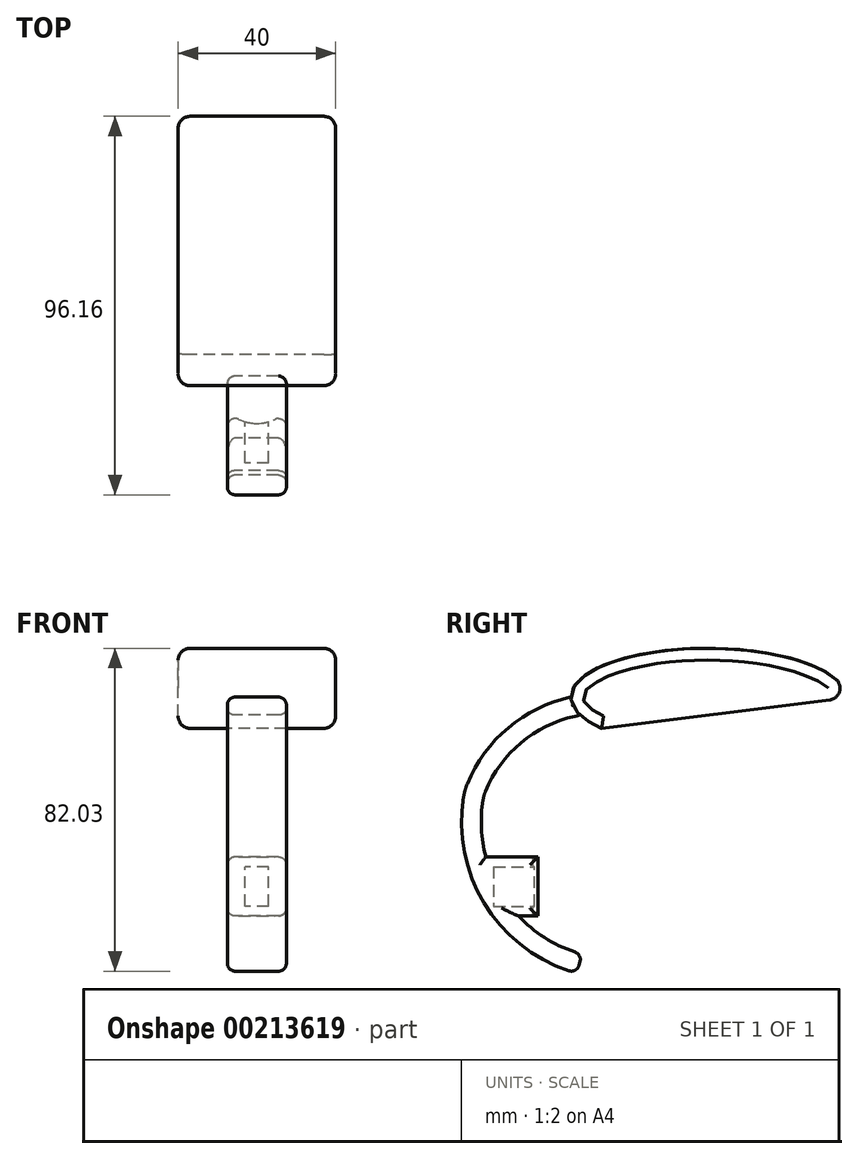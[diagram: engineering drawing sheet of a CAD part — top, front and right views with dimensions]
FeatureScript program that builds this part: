
annotation { "Feature Type Name" : "Feature", "Feature Type Description" : "" }
export const myFeature = defineFeature(function(context is Context, id is Id, definition is map)
    precondition{}
    {
        {
            var Q0;
            Q0=qCreatedBy(makeId("Right.planeOp"),FACE);
            var sketch = newSketch(context, id + "F0", { "sketchPlane" : qUnion([Q0])});
            skPoint(sketch, "E0", {"position": v(-25.02, -24.7) * mm});
            skPoint(sketch, "E1", {"position": v(-49.96, 15.62) * mm});
            skPoint(sketch, "E2", {"position": v(-17.82, 36.4) * mm});
            skPoint(sketch, "E3", {"position": v(-45.62, -9.14) * mm});
            skPoint(sketch, "E4", {"position": v(-37.55, 31.22) * mm});
            skArc(sketch, "E5", {"start": v(-50.16, 14.52) * mm, "mid": v(-45.13, -9.93) * mm, "end": v(-25.02, -24.7) * mm});
            skArc(sketch, "E6", {"start": v(-26.84, 35.73) * mm, "mid": v(-40.53, 29) * mm, "end": v(-49.54, 16.68) * mm});
            skArc(sketch, "E7.filletArc", {"start": v(-49.54, 16.68) * mm, "mid": v(-49.91, 15.62) * mm, "end": v(-50.16, 14.52) * mm});
            skArc(sketch, "E8.0", {"start": v(-27.9, 40.62) * mm, "mid": v(-43.75, 32.83) * mm, "end": v(-54.17, 18.59) * mm});
            skArc(sketch, "E9.0", {"start": v(-55.1, 15.33) * mm, "mid": v(-49.34, -12.62) * mm, "end": v(-26.34, -29.53) * mm});
            skArc(sketch, "E9.1", {"start": v(-54.17, 18.59) * mm, "mid": v(-54.72, 16.99) * mm, "end": v(-55.1, 15.33) * mm});
            skLineSegment(sketch, "E10", {"start": v(-26.34, -29.53) * mm, "end": v(-25.02, -24.7) * mm});
            skLineSegment(sketch, "E11", {"start": v(-26.84, 35.73) * mm, "end": v(22, 46.42) * mm});
            skLineSegment(sketch, "E12.0", {"start": v(-27.9, 40.62) * mm, "end": v(20.94, 51.3) * mm});
            skLineSegment(sketch, "E13", {"start": v(20.94, 51.3) * mm, "end": v(22, 46.42) * mm});
            skEllipticalArc(sketch, "E14", {});
            skLineSegment(sketch, "E15", {"start": v(-20.03, 32.68) * mm, "end": v(42.1, 40.43) * mm});
            skPoint(sketch, "E15.endSnap0", {"position": v(42.1, 40.4) * mm});
            skLineSegment(sketch, "E16", {"start": v(-46.55, -7.5) * mm, "end": v(-34.49, -7.5) * mm, "construction": true});
            skLineSegment(sketch, "E17.bottom", {"start": v(-49.49, 0) * mm, "end": v(-34.49, 0) * mm});
            skLineSegment(sketch, "E17.right", {"start": v(-34.49, 0) * mm, "end": v(-34.49, -15) * mm});
            skLineSegment(sketch, "E18.trimOffspring", {"start": v(-41.17, -15) * mm, "end": v(-34.49, -15) * mm});
            const initialGuessF0  = {"E14": [0.007094516884535551, 0.040509749203920364, -0.9999952117273706, 0.0030945956652309804, 0.035, 0.0125, 3.141592653589793, 0.6850566038234638]};
            skSetInitialGuess(sketch, initialGuessF0);
            skSolve(sketch);
        }
        {
            var Q0;
            Q0=makeQuery(id+"F0.imprint","IMPRINT",FACE,{"disambiguationData":[TD([[makeQuery(id+"F0.imprint","IMPRINT",EDGE,{"derivedFrom":sQuery(id+"F0.wireOp",EDGE,"E5")}),-1.0]])]});
            var Q1;
            {var subQ0=sQuery(id+"F0.wireOp",EDGE,"E17.bottom");Q1=makeQuery(id+"F0.imprint","IMPRINT",FACE,{"disambiguationData":[TD([[makeQuery(id+"F0.imprint","IMPRINT",EDGE,{"derivedFrom":subQ0}),-1.0]])]});}
            extrude(context, id + "F1", {"entities" : qUnion([Q0, Q1]), "endBound" : BoundingType.SYMMETRIC, "depth" : 15 * mm});
        }
        {
            var Q0;
            {var subQ4=sQuery(id+"F0.wireOp",EDGE,"E12.0");Q0=makeQuery(id+"F0.imprint","IMPRINT",FACE,{"disambiguationData":[TD([[makeQuery(id+"F0.imprint","IMPRINT",EDGE,{"derivedFrom":subQ4}),1.0]])]});}
            var Q1;
            {var subQ4=sQuery(id+"F0.wireOp",EDGE,"E12.0");Q1=makeQuery(id+"F0.imprint","IMPRINT",FACE,{"disambiguationData":[TD([[makeQuery(id+"F0.imprint","IMPRINT",EDGE,{"derivedFrom":subQ4}),-1.0]])]});}
            extrude(context, id + "F2", {"entities" : qUnion([Q0, Q1]), "operationType" : NewBodyOperationType.ADD, "endBound" : BoundingType.SYMMETRIC, "depth" : 40 * mm});
        }
        {
            var Q0;
            Q0=makeQuery(id+"F1.opExtrude","SWEPT_EDGE",EDGE,{"disambiguationData":[OSD([sQuery(id+"F0.wireOp",EDGE,"E5"),sQuery(id+"F0.wireOp",EDGE,"E10")])]});
            var Q1;
            Q1=makeQuery(id+"F1.opExtrude","SWEPT_EDGE",EDGE,{"disambiguationData":[OSD([sQuery(id+"F0.wireOp",EDGE,"E9.0"),sQuery(id+"F0.wireOp",EDGE,"E10")])]});
            var Q2;
            Q2=makeQuery(id+"F1.opExtrude","CAP_EDGE",EDGE,{"disambiguationData":[OSD([sQuery(id+"F0.wireOp",EDGE,"E10")])],"isStart":false});
            var Q3;
            Q3=makeQuery(id+"F1.opExtrude","CAP_EDGE",EDGE,{"disambiguationData":[OSD([sQuery(id+"F0.wireOp",EDGE,"E10")])],"isStart":true});
            var Q4;
            Q4=makeQuery(id+"F1.opExtrude","CAP_EDGE",EDGE,{"disambiguationData":[OSD([sQuery(id+"F0.wireOp",EDGE,"E9.0")])],"isStart":false});
            var Q5;
            Q5=makeQuery(id+"F1.opExtrude","CAP_EDGE",EDGE,{"disambiguationData":[OSD([sQuery(id+"F0.wireOp",EDGE,"E5")])],"isStart":false});
            var Q6;
            Q6=makeQuery(id+"F1.opExtrude","CAP_EDGE",EDGE,{"disambiguationData":[OSD([sQuery(id+"F0.wireOp",EDGE,"E5")])],"isStart":true});
            var Q7;
            Q7=makeQuery(id+"F1.opExtrude","CAP_EDGE",EDGE,{"disambiguationData":[OSD([sQuery(id+"F0.wireOp",EDGE,"E9.0")])],"isStart":true});
            fillet(context, id + "F3", {"entities" : qUnion([Q0, Q1, Q2, Q3, Q4, Q5, Q6, Q7]), "radius" : 2 * mm, "tangentPropagation" : true, "allowEdgeOverflow" : false});
        }
        {
            var Q0;
            Q0=makeQuery(id+"F2.opExtrude","CAP_EDGE",EDGE,{"disambiguationData":[OSD([sQuery(id+"F0.wireOp",EDGE,"E14")])],"isStart":false});
            var Q1;
            Q1=makeQuery(id+"F2.opExtrude","CAP_EDGE",EDGE,{"disambiguationData":[OSD([sQuery(id+"F0.wireOp",EDGE,"E14")])],"isStart":true});
            var Q2;
            {var subQ0=sQuery(id+"F0.wireOp",EDGE,"E15");var subQ1=sQuery(id+"F0.wireOp",EDGE,"E14");Q2=makeQuery(id+"F2.opExtrude","SWEPT_EDGE",EDGE,{"disambiguationData":[OSD([subQ1,subQ0]),TDD([makeQuery(id+"F0.imprint","INTERSECT",VERTEX,{"disambiguationData":[OD(1.0)],"derivedFrom":[subQ1,subQ0]})])]});}
            var Q3;
            Q3=makeQuery(id+"F1.opExtrude","SWEPT_EDGE",EDGE,{"disambiguationData":[OSD([sQuery(id+"F0.wireOp",EDGE,"E8.0"),sQuery(id+"F0.wireOp",EDGE,"E12.0"),sQuery(id+"F0.wireOp",EDGE,"E14")])]});
            var Q4;
            Q4=makeQuery(id+"F1.opExtrude","SWEPT_EDGE",EDGE,{"disambiguationData":[OSD([sQuery(id+"F0.wireOp",EDGE,"E11"),sQuery(id+"F0.wireOp",EDGE,"E14")])]});
            var Q5;
            Q5=makeQuery(id+"F1.opExtrude","CAP_EDGE",EDGE,{"disambiguationData":[OSD([sQuery(id+"F0.wireOp",EDGE,"E14")])],"isStart":false});
            var Q6;
            Q6=makeQuery(id+"F1.opExtrude","CAP_EDGE",EDGE,{"disambiguationData":[OSD([sQuery(id+"F0.wireOp",EDGE,"E14")])],"isStart":true});
            var Q7;
            Q7=makeQuery(id+"F2.opExtrude","CAP_EDGE",EDGE,{"disambiguationData":[OSD([sQuery(id+"F0.wireOp",EDGE,"E15")])],"isStart":false});
            var Q8;
            Q8=makeQuery(id+"F2.opExtrude","CAP_EDGE",EDGE,{"disambiguationData":[OSD([sQuery(id+"F0.wireOp",EDGE,"E15")])],"isStart":true});
            fillet(context, id + "F4", {"entities" : qUnion([Q0, Q1, Q2, Q3, Q4, Q5, Q6, Q7, Q8]), "radius" : 3 * mm, "tangentPropagation" : true, "allowEdgeOverflow" : false});
        }
        {
            var Q0;
            Q0=makeQuery(id+"F1.opExtrude","SWEPT_FACE",FACE,{"disambiguationData":[OSD([sQuery(id+"F0.wireOp",EDGE,"E17.right")])]});
            var sketch = newSketch(context, id + "F5", { "sketchPlane" : qUnion([Q0])});
            skLineSegment(sketch, "E19.bottom", {"start": v(-3, -2.5) * mm, "end": v(3, -2.5) * mm});
            skLineSegment(sketch, "E19.top", {"start": v(-3, -12.5) * mm, "end": v(3, -12.5) * mm});
            skLineSegment(sketch, "E19.left", {"start": v(-3, -2.5) * mm, "end": v(-3, -12.5) * mm});
            skLineSegment(sketch, "E19.right", {"start": v(3, -2.5) * mm, "end": v(3, -12.5) * mm});
            skPoint(sketch, "E19.middle", {"position": v(0, -7.5) * mm});
            skSolve(sketch);
        }
        {
            var Q0;
            Q0 = qSketchRegion(id + "F5", true);
            extrude(context, id + "F6", {"entities" : qUnion([Q0]), "operationType" : NewBodyOperationType.REMOVE, "oppositeDirection" : true, "depth" : 13 * mm});
        }
        {
            var Q0;
            Q0=makeQuery(id+"F1.opExtrude","SWEPT_FACE",FACE,{"disambiguationData":[OSD([sQuery(id+"F0.wireOp",EDGE,"E17.bottom")])]});
            var sketch = newSketch(context, id + "F7", { "sketchPlane" : qUnion([Q0])});
            skLineSegment(sketch, "E20", {"start": v(0, -34.49) * mm, "end": v(0, -37.49) * mm, "construction": true});
            skArc(sketch, "E21", {"start": v(-7.5, -34.49) * mm, "mid": v(0, -37.49) * mm, "end": v(7.5, -34.49) * mm});
            skLineSegment(sketch, "E22", {"start": v(-7.5, -34.49) * mm, "end": v(7.5, -34.49) * mm});
            skSolve(sketch);
        }
        {
            var Q0;
            Q0 = qSketchRegion(id + "F7", true);
            extrude(context, id + "F8", {"entities" : qUnion([Q0]), "operationType" : NewBodyOperationType.REMOVE, "oppositeDirection" : true, "depth" : 15 * mm});
        }
        {
            var Q0;
            Q0=makeQuery(id+"F1.opExtrude","CAP_EDGE",EDGE,{"disambiguationData":[OSD([sQuery(id+"F0.wireOp",EDGE,"E17.bottom")])],"isStart":false});
            var Q1;
            Q1=makeQuery(id+"F1.opExtrude","CAP_EDGE",EDGE,{"disambiguationData":[OSD([sQuery(id+"F0.wireOp",EDGE,"E17.bottom")])],"isStart":true});
            var Q2;
            {var subQ0=sQuery(id+"F7.wireOp",EDGE,"E22");var subQ1=sQuery(id+"F7.wireOp",EDGE,"E21");var subQ2=sQuery(id+"F0.wireOp",EDGE,"E17.bottom");Q2=makeQuery(id+"F8.boolean.opBoolean","MERGE",EDGE,{"derivedFrom":[makeQuery(id+"F1.opExtrude","CAP_EDGE",EDGE,{"disambiguationData":[OSD([sQuery(id+"F0.wireOp",EDGE,"E17.right")])],"isStart":true}),makeQuery(id+"F8.opExtrude","SWEPT_EDGE",EDGE,{"disambiguationData":[OSD([subQ2,subQ1,subQ0]),TDD([makeQuery(id+"F7.imprint","INTERSECT",VERTEX,{"derivedFrom":[makeQuery(id+"F1.opExtrude","CAP_EDGE",EDGE,{"disambiguationData":[OSD([subQ2])],"isStart":true}),subQ1,subQ0]})])]})]});}
            var Q3;
            {var subQ0=sQuery(id+"F7.wireOp",EDGE,"E22");var subQ1=sQuery(id+"F7.wireOp",EDGE,"E21");var subQ2=sQuery(id+"F0.wireOp",EDGE,"E17.bottom");Q3=makeQuery(id+"F8.boolean.opBoolean","MERGE",EDGE,{"derivedFrom":[makeQuery(id+"F1.opExtrude","CAP_EDGE",EDGE,{"disambiguationData":[OSD([sQuery(id+"F0.wireOp",EDGE,"E17.right")])],"isStart":false}),makeQuery(id+"F8.opExtrude","SWEPT_EDGE",EDGE,{"disambiguationData":[OSD([subQ2,subQ1,subQ0]),TDD([makeQuery(id+"F7.imprint","INTERSECT",VERTEX,{"derivedFrom":[makeQuery(id+"F1.opExtrude","CAP_EDGE",EDGE,{"disambiguationData":[OSD([subQ2])],"isStart":false}),subQ1,subQ0]})])]})]});}
            var Q4;
            Q4=makeQuery(id+"F1.opExtrude","CAP_EDGE",EDGE,{"disambiguationData":[OSD([sQuery(id+"F0.wireOp",EDGE,"E18.trimOffspring")])],"isStart":false});
            var Q5;
            Q5=makeQuery(id+"F1.opExtrude","CAP_EDGE",EDGE,{"disambiguationData":[OSD([sQuery(id+"F0.wireOp",EDGE,"E18.trimOffspring")])],"isStart":true});
            fillet(context, id + "F9", {"entities" : qUnion([Q0, Q1, Q2, Q3, Q4, Q5]), "radius" : 2 * mm, "tangentPropagation" : true, "allowEdgeOverflow" : false});
        }
    });
